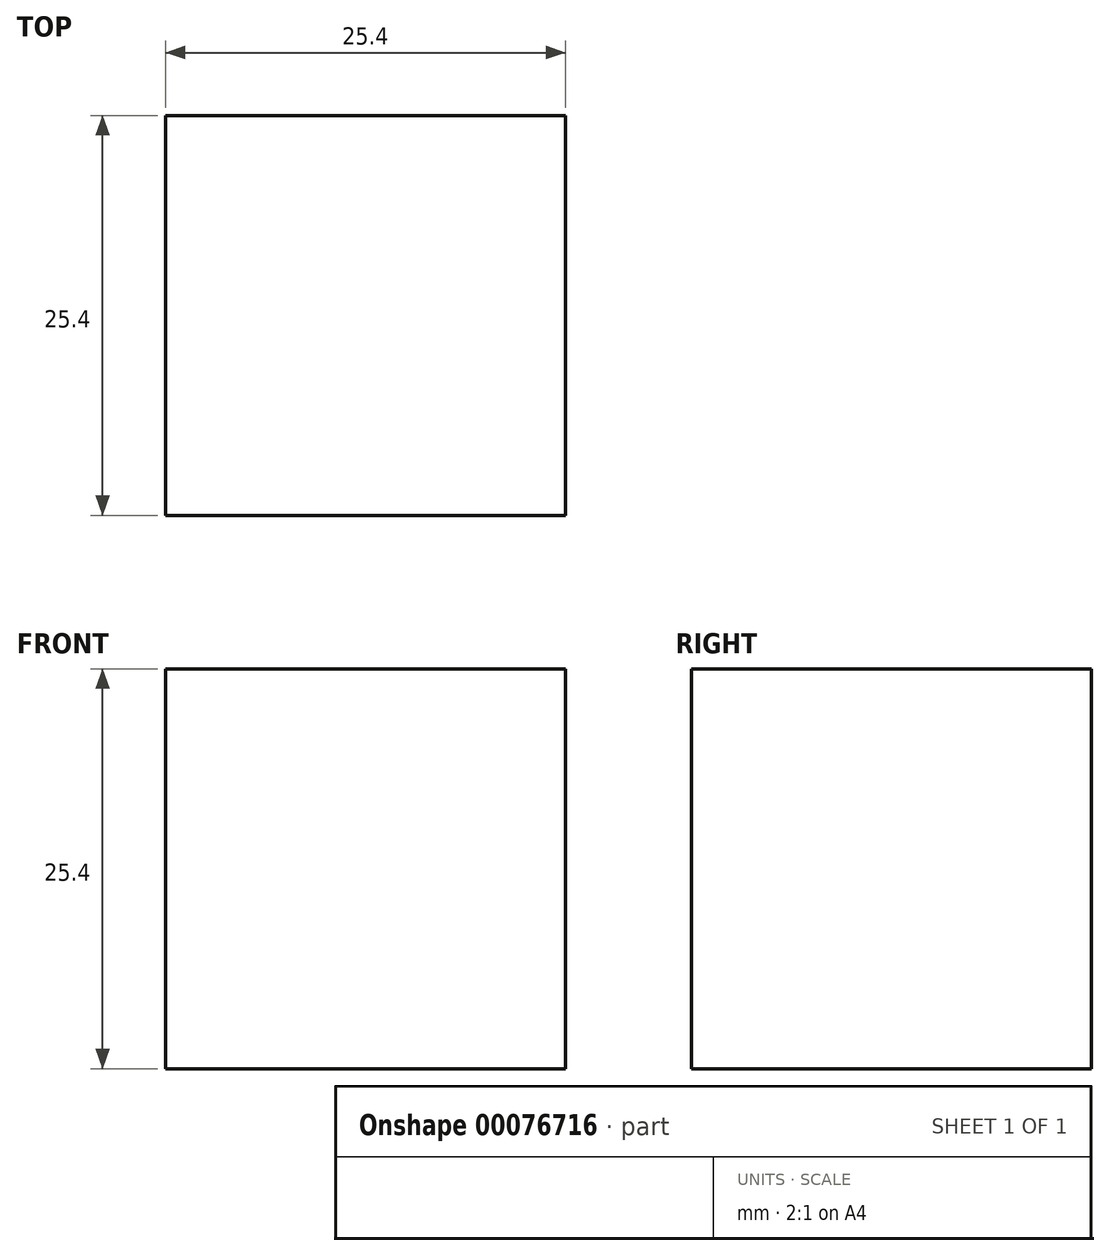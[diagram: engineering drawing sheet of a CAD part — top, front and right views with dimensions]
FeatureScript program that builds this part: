
annotation { "Feature Type Name" : "Feature", "Feature Type Description" : "" }
export const myFeature = defineFeature(function(context is Context, id is Id, definition is map)
    precondition{}
    {
        {
            var Q0;
            Q0=qCreatedBy(makeId("Top.planeOp"),FACE);
            var sketch = newSketch(context, id + "F0", { "sketchPlane" : qUnion([Q0])});
            skLineSegment(sketch, "E0.bottom", {"start": v(-12.7, 12.7) * mm, "end": v(12.7, 12.7) * mm});
            skLineSegment(sketch, "E0.top", {"start": v(-12.7, -12.7) * mm, "end": v(12.7, -12.7) * mm});
            skLineSegment(sketch, "E0.left", {"start": v(-12.7, 12.7) * mm, "end": v(-12.7, -12.7) * mm});
            skLineSegment(sketch, "E0.right", {"start": v(12.7, 12.7) * mm, "end": v(12.7, -12.7) * mm});
            skPoint(sketch, "E0.middle", {"position": v(0, 0) * mm});
            skSolve(sketch);
        }
        {
            var Q0;
            Q0=makeQuery(id+"F0.imprint","IMPRINT",FACE,{"disambiguationData":[TD([[makeQuery(id+"F0.imprint","IMPRINT",EDGE,{"derivedFrom":sQuery(id+"F0.wireOp",EDGE,"E0.bottom")}),-1.0]])]});
            extrude(context, id + "F1", {"entities" : qUnion([Q0]), "depth" : 25.4 * mm});
        }
    });
